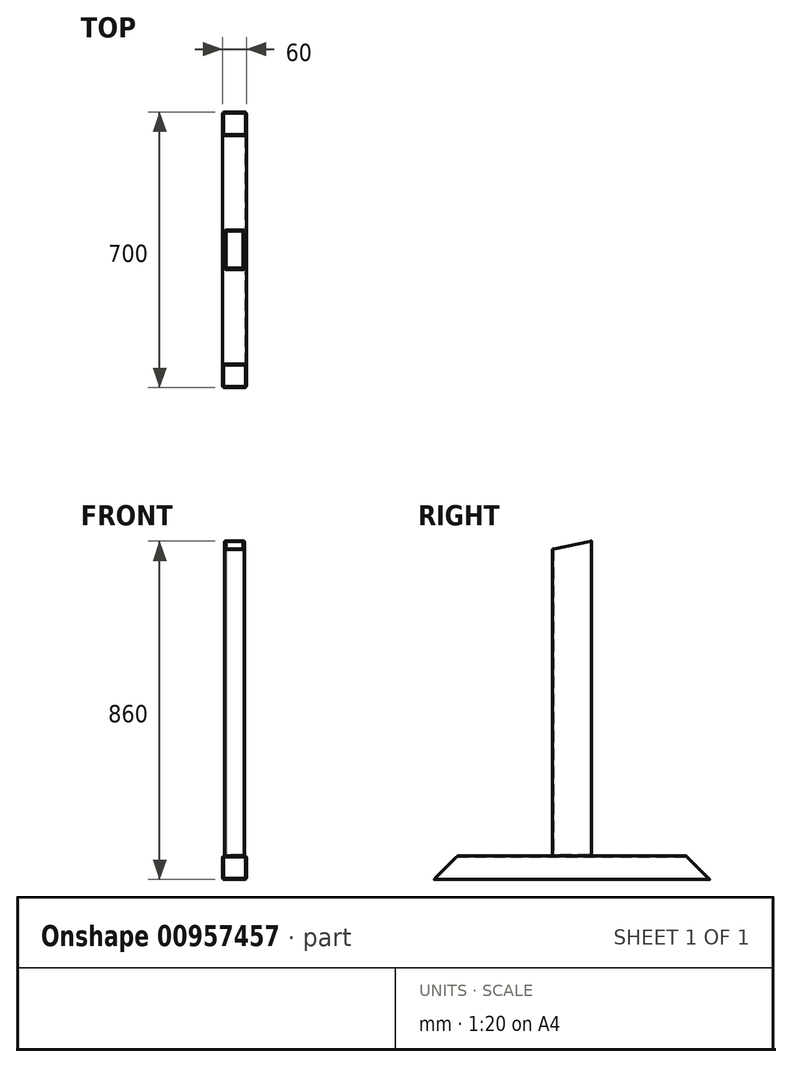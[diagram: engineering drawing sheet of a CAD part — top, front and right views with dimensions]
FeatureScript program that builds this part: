
annotation { "Feature Type Name" : "Feature", "Feature Type Description" : "" }
export const myFeature = defineFeature(function(context is Context, id is Id, definition is map)
    precondition{}
    {
        {
            var Q0;
            Q0=qCreatedBy(makeId("Top.planeOp"),FACE);
            var sketch = newSketch(context, id + "F0", { "sketchPlane" : qUnion([Q0])});
            skLineSegment(sketch, "E0.bottom", {"start": v(30, -350) * mm, "end": v(-30, -350) * mm});
            skLineSegment(sketch, "E0.top", {"start": v(30, 350) * mm, "end": v(-30, 350) * mm});
            skLineSegment(sketch, "E0.left", {"start": v(30, -350) * mm, "end": v(30, 350) * mm});
            skLineSegment(sketch, "E0.right", {"start": v(-30, -350) * mm, "end": v(-30, 350) * mm});
            skPoint(sketch, "E0.middle", {"position": v(0, 0) * mm});
            skSolve(sketch);
        }
        {
            var Q0;
            Q0 = qSketchRegion(id + "F0", true);
            extrude(context, id + "F1", {"entities" : qUnion([Q0]), "depth" : 60 * mm, "offsetDistance" : 25 * mm});
        }
        {
            var Q0;
            Q0=makeQuery(id+"F1.opExtrude","CAP_EDGE",EDGE,{"disambiguationData":[OSD([sQuery(id+"F0.wireOp",EDGE,"E0.bottom")])],"isStart":false});
            var Q1;
            Q1=makeQuery(id+"F1.opExtrude","CAP_EDGE",EDGE,{"disambiguationData":[OSD([sQuery(id+"F0.wireOp",EDGE,"E0.top")])],"isStart":false});
            chamfer(context, id + "F2", {"entities" : qUnion([Q0, Q1]), "width" : 60 * mm, "tangentPropagation" : true});
        }
        {
            var Q0;
            Q0=makeQuery(id+"F2.opChamfer","BLEND_FACE",FACE,{"disambiguationData":[OSD([sQuery(id+"F0.wireOp",EDGE,"E0.bottom")])]});
            var Q1;
            Q1=makeQuery(id+"F2.opChamfer","BLEND_FACE",FACE,{"disambiguationData":[OSD([sQuery(id+"F0.wireOp",EDGE,"E0.top")])]});
            shell(context, id + "F3", {"entities" : qUnion([Q0, Q1]), "thickness" : 2.5 * mm});
        }
        {
            var Q0;
            Q0=makeQuery(id+"F1.opExtrude","CAP_FACE",FACE,{"disambiguationData":[OSD([sQuery(id+"F0.wireOp",EDGE,"E0.bottom"),sQuery(id+"F0.wireOp",EDGE,"E0.top"),sQuery(id+"F0.wireOp",EDGE,"E0.left"),sQuery(id+"F0.wireOp",EDGE,"E0.right")])],"isStart":false});
            var sketch = newSketch(context, id + "F4", { "sketchPlane" : qUnion([Q0])});
            skLineSegment(sketch, "E1.bottom", {"start": v(25, 50) * mm, "end": v(-25, 50) * mm});
            skLineSegment(sketch, "E1.top", {"start": v(25, -50) * mm, "end": v(-25, -50) * mm});
            skLineSegment(sketch, "E1.left", {"start": v(25, 50) * mm, "end": v(25, -50) * mm});
            skLineSegment(sketch, "E1.right", {"start": v(-25, 50) * mm, "end": v(-25, -50) * mm});
            skPoint(sketch, "E1.middle", {"position": v(0, 0) * mm});
            skSolve(sketch);
        }
        {
            var Q0;
            Q0=makeQuery(id+"F4.imprint","IMPRINT",FACE,{"disambiguationData":[TD([[makeQuery(id+"F4.imprint","IMPRINT",EDGE,{"derivedFrom":sQuery(id+"F4.wireOp",EDGE,"E1.bottom")}),1.0]])]});
            extrude(context, id + "F5", {"entities" : qUnion([Q0]), "depth" : 800 * mm, "offsetDistance" : 25 * mm});
        }
        {
            var Q0;
            Q0=makeQuery(id+"F5.opExtrude","SWEPT_EDGE",EDGE,{"disambiguationData":[OSD([sQuery(id+"F4.wireOp",EDGE,"E1.bottom"),sQuery(id+"F4.wireOp",EDGE,"E1.right")])]});
            var Q1;
            Q1=makeQuery(id+"F5.opExtrude","SWEPT_EDGE",EDGE,{"disambiguationData":[OSD([sQuery(id+"F4.wireOp",EDGE,"E1.bottom"),sQuery(id+"F4.wireOp",EDGE,"E1.left")])]});
            var Q2;
            Q2=makeQuery(id+"F1.opExtrude","CAP_EDGE",EDGE,{"disambiguationData":[OSD([sQuery(id+"F0.wireOp",EDGE,"E0.right")])],"isStart":false});
            var Q3;
            Q3=makeQuery(id+"F1.opExtrude","CAP_EDGE",EDGE,{"disambiguationData":[OSD([sQuery(id+"F0.wireOp",EDGE,"E0.left")])],"isStart":false});
            var Q4;
            Q4=makeQuery(id+"F5.opExtrude","SWEPT_EDGE",EDGE,{"disambiguationData":[OSD([sQuery(id+"F4.wireOp",EDGE,"E1.top"),sQuery(id+"F4.wireOp",EDGE,"E1.right")])]});
            var Q5;
            Q5=makeQuery(id+"F5.opExtrude","SWEPT_EDGE",EDGE,{"disambiguationData":[OSD([sQuery(id+"F4.wireOp",EDGE,"E1.top"),sQuery(id+"F4.wireOp",EDGE,"E1.left")])]});
            var Q6;
            Q6=makeQuery(id+"F1.opExtrude","CAP_EDGE",EDGE,{"disambiguationData":[OSD([sQuery(id+"F0.wireOp",EDGE,"E0.right")])],"isStart":true});
            var Q7;
            Q7=makeQuery(id+"F1.opExtrude","CAP_EDGE",EDGE,{"disambiguationData":[OSD([sQuery(id+"F0.wireOp",EDGE,"E0.left")])],"isStart":true});
            fillet(context, id + "F6", {"entities" : qUnion([Q0, Q1, Q2, Q3, Q4, Q5, Q6, Q7]), "radius" : 4 * mm, "tangentPropagation" : true, "allowEdgeOverflow" : false});
        }
        {
            var Q0;
            Q0=makeQuery(id+"F5.opExtrude","CAP_FACE",FACE,{"disambiguationData":[OSD([sQuery(id+"F4.wireOp",EDGE,"E1.bottom"),sQuery(id+"F4.wireOp",EDGE,"E1.top"),sQuery(id+"F4.wireOp",EDGE,"E1.left"),sQuery(id+"F4.wireOp",EDGE,"E1.right")])],"isStart":false});
            shell(context, id + "F7", {"entities" : qUnion([Q0]), "thickness" : 3 * mm});
        }
        {
            var Q0;
            Q0=makeQuery(id+"F5.opExtrude","CAP_EDGE",EDGE,{"disambiguationData":[OSD([sQuery(id+"F4.wireOp",EDGE,"E1.top")])],"isStart":false});
            chamfer(context, id + "F8", {"entities" : qUnion([Q0]), "chamferType" : ChamferType.OFFSET_ANGLE, "width" : 100 * mm, "oppositeDirection" : true, "angle" : 12 * degree});
        }
    });
